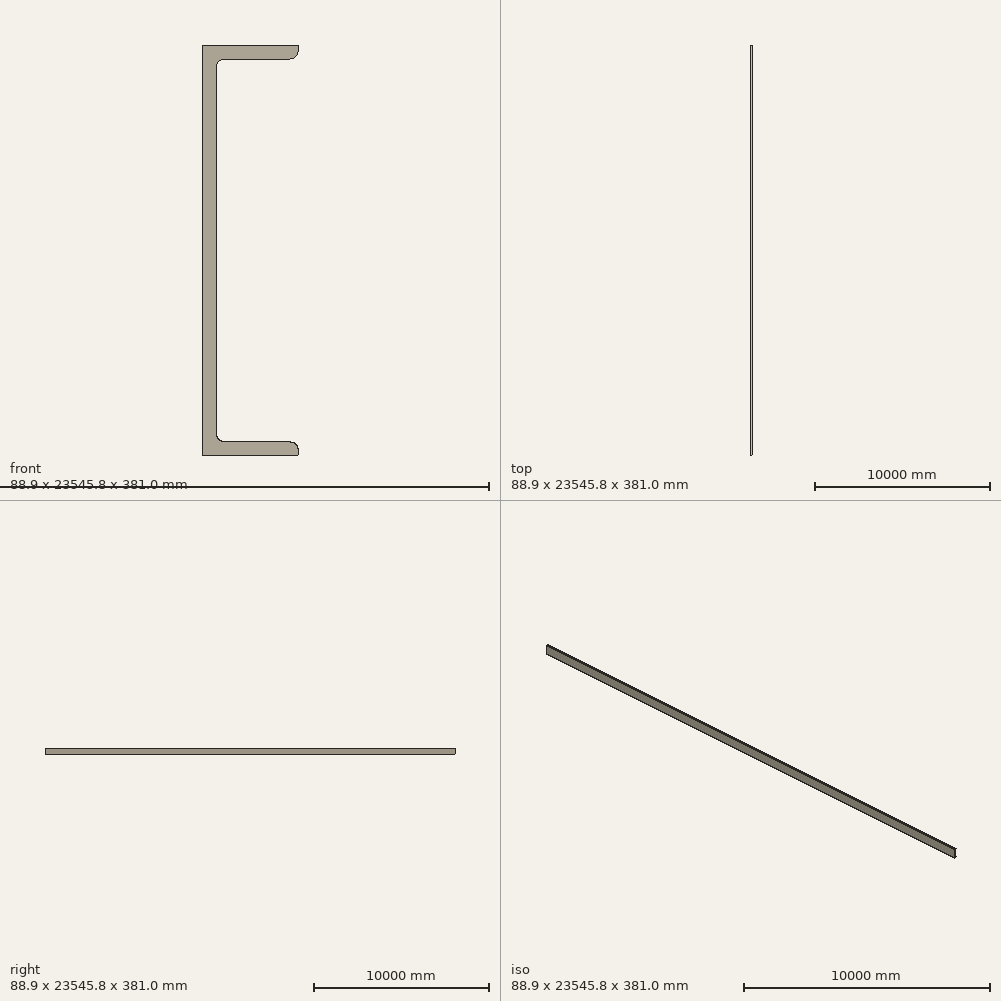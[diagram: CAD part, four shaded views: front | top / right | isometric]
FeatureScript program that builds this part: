
annotation { "Feature Type Name" : "Feature", "Feature Type Description" : "" }
export const myFeature = defineFeature(function(context is Context, id is Id, definition is map)
    precondition{}
    {
        {
            var Q0;
            Q0=qCreatedBy(makeId("Front.planeOp"),FACE);
            var sketch = newSketch(context, id + "F0", { "sketchPlane" : qUnion([Q0])});
            skLineSegment(sketch, "E0", {"start": v(44.45, 190.5) * mm, "end": v(-44.45, 190.5) * mm});
            skLineSegment(sketch, "E1", {"start": v(-44.45, 190.5) * mm, "end": v(-44.45, -190.5) * mm});
            skLineSegment(sketch, "E2", {"start": v(-44.45, -190.5) * mm, "end": v(44.45, -190.5) * mm});
            skLineSegment(sketch, "E3", {"start": v(44.45, -190.5) * mm, "end": v(44.45, -177.8) * mm});
            skLineSegment(sketch, "E4", {"start": v(44.45, -177.8) * mm, "end": v(-31.75, -177.8) * mm});
            skLineSegment(sketch, "E5", {"start": v(-31.75, -177.8) * mm, "end": v(-31.75, 177.8) * mm});
            skLineSegment(sketch, "E6", {"start": v(-31.75, 177.8) * mm, "end": v(44.45, 177.8) * mm});
            skLineSegment(sketch, "E7", {"start": v(44.45, 177.8) * mm, "end": v(44.45, 190.5) * mm});
            skSolve(sketch);
        }
        {
            var Q0;
            Q0=makeQuery(id+"F0.imprint","IMPRINT",FACE,{"disambiguationData":[TD([[makeQuery(id+"F0.imprint","IMPRINT",EDGE,{"derivedFrom":sQuery(id+"F0.wireOp",EDGE,"E0")}),1.0]])]});
            extrude(context, id + "F1", {"entities" : qUnion([Q0]), "depth" : 23545.8 * mm, "offsetDistance" : 25.4 * mm});
        }
        {
            var Q0;
            Q0=makeQuery(id+"F1.opExtrude","SWEPT_EDGE",EDGE,{"disambiguationData":[OSD([sQuery(id+"F0.wireOp",EDGE,"E3"),sQuery(id+"F0.wireOp",EDGE,"E4")])]});
            var Q1;
            Q1=makeQuery(id+"F1.opExtrude","SWEPT_EDGE",EDGE,{"disambiguationData":[OSD([sQuery(id+"F0.wireOp",EDGE,"E4"),sQuery(id+"F0.wireOp",EDGE,"E5")])]});
            var Q2;
            Q2=makeQuery(id+"F1.opExtrude","SWEPT_EDGE",EDGE,{"disambiguationData":[OSD([sQuery(id+"F0.wireOp",EDGE,"E5"),sQuery(id+"F0.wireOp",EDGE,"E6")])]});
            var Q3;
            Q3=makeQuery(id+"F1.opExtrude","SWEPT_EDGE",EDGE,{"disambiguationData":[OSD([sQuery(id+"F0.wireOp",EDGE,"E6"),sQuery(id+"F0.wireOp",EDGE,"E7")])]});
            fillet(context, id + "F2", {"entities" : qUnion([Q0, Q1, Q2, Q3]), "radius" : 7.62 * mm, "tangentPropagation" : true, "allowEdgeOverflow" : false});
        }
    });
